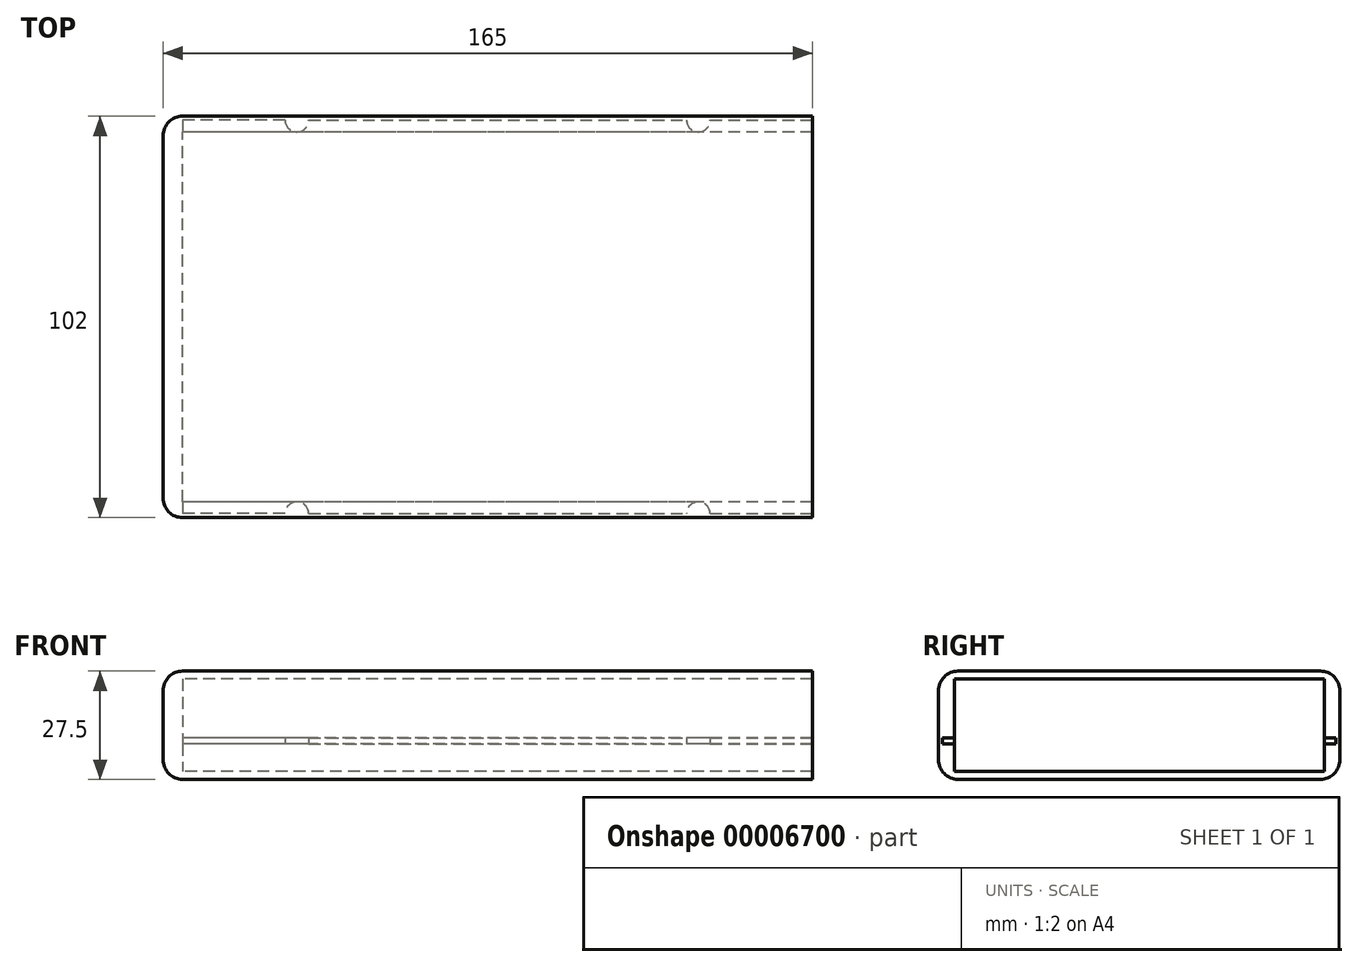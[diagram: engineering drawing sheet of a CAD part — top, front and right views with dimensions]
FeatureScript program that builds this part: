
annotation { "Feature Type Name" : "Feature", "Feature Type Description" : "" }
export const myFeature = defineFeature(function(context is Context, id is Id, definition is map)
    precondition{}
    {
        {
            var Q0;
            Q0=qCreatedBy(makeId("Top.planeOp"),FACE);
            var sketch = newSketch(context, id + "F0", { "sketchPlane" : qUnion([Q0])});
            skLineSegment(sketch, "E0.left", {"start": v(-80, 50) * mm, "end": v(-80, -50) * mm});
            skLineSegment(sketch, "E0.right", {"start": v(80, 50) * mm, "end": v(80, -50) * mm});
            skLineSegment(sketch, "E1.bottom", {"start": v(-87, -17.5) * mm, "end": v(-80, -17.5) * mm});
            skLineSegment(sketch, "E1.top", {"start": v(-87, -33) * mm, "end": v(-80, -33) * mm});
            skLineSegment(sketch, "E1.left", {"start": v(-87, -17.5) * mm, "end": v(-87, -33) * mm});
            skLineSegment(sketch, "E1.right", {"start": v(-80, -17.5) * mm, "end": v(-80, -33) * mm});
            skArc(sketch, "E2", {"start": v(54, 50) * mm, "mid": v(51, 47) * mm, "end": v(48, 50) * mm});
            skLineSegment(sketch, "E3", {"start": v(54, 50) * mm, "end": v(80, 50) * mm});
            skArc(sketch, "E4.MirrorCS", {"start": v(-54, 50) * mm, "mid": v(-51, 47) * mm, "end": v(-48, 50) * mm});
            skLineSegment(sketch, "E5.MirrorCS", {"start": v(-54, 50) * mm, "end": v(-80, 50) * mm});
            skLineSegment(sketch, "E6", {"start": v(-48, 50) * mm, "end": v(48, 50) * mm});
            skLineSegment(sketch, "E7.MirrorCS", {"start": v(54, -50) * mm, "end": v(80, -50) * mm});
            skArc(sketch, "E8.MirrorCS", {"start": v(54, -50) * mm, "mid": v(51, -47) * mm, "end": v(48, -50) * mm});
            skLineSegment(sketch, "E9.MirrorCS", {"start": v(-48, -50) * mm, "end": v(48, -50) * mm});
            skArc(sketch, "E10.MirrorCS", {"start": v(-54, -50) * mm, "mid": v(-51, -47) * mm, "end": v(-48, -50) * mm});
            skLineSegment(sketch, "E11.MirrorCS", {"start": v(-54, -50) * mm, "end": v(-80, -50) * mm});
            skLineSegment(sketch, "E12", {"start": v(48, 50) * mm, "end": v(54, 50) * mm, "construction": true});
            skSolve(sketch);
        }
        {
            var Q0;
            Q0=makeQuery(id+"F0.imprint","IMPRINT",FACE,{"disambiguationData":[TD([[makeQuery(id+"F0.imprint","IMPRINT",EDGE,{"derivedFrom":sQuery(id+"F0.wireOp",EDGE,"E0.right")}),-1.0]])]});
            extrude(context, id + "F1", {"entities" : qUnion([Q0]), "depth" : 1.5 * mm});
        }
        {
            var Q0;
            Q0=qCreatedBy(makeId("Right.planeOp"),FACE);
            var sketch = newSketch(context, id + "F2", { "sketchPlane" : qUnion([Q0])});
            skLineSegment(sketch, "E13.bottom", {"start": v(-47, 16.5) * mm, "end": v(47, 16.5) * mm});
            skLineSegment(sketch, "E13.top", {"start": v(-47, -7) * mm, "end": v(47, -7) * mm});
            skLineSegment(sketch, "E13.left", {"start": v(-47, 16.5) * mm, "end": v(-47, -7) * mm});
            skLineSegment(sketch, "E13.right", {"start": v(47, 16.5) * mm, "end": v(47, -7) * mm});
            skSolve(sketch);
        }
        {
            var Q0;
            Q0=makeQuery(id+"F2.imprint","IMPRINT",FACE,{"disambiguationData":[TD([[makeQuery(id+"F2.imprint","IMPRINT",EDGE,{"derivedFrom":sQuery(id+"F2.wireOp",EDGE,"E13.bottom")}),-1.0]])]});
            var Q1;
            Q1=makeQuery(id+"F1.opExtrude","SWEPT_FACE",FACE,{"disambiguationData":[OSD([sQuery(id+"F0.wireOp",EDGE,"E0.right")])]});
            var Q2;
            Q2=makeQuery(id+"F1.opExtrude","SWEPT_FACE",FACE,{"disambiguationData":[OSD([sQuery(id+"F0.wireOp",EDGE,"E0.left"),sQuery(id+"F0.wireOp",EDGE,"E1.right")])]});
            extrude(context, id + "F3", {"entities" : qUnion([Q0]), "endBound" : BoundingType.UP_TO_SURFACE, "endBoundEntityFace" : qUnion([Q1]), "depth" : 25 * mm, "hasSecondDirection" : true, "secondDirectionBound" : SecondDirectionBoundingType.UP_TO_SURFACE, "secondDirectionOppositeDirection" : true, "secondDirectionBoundEntityFace" : qUnion([Q2]), "secondDirectionDepth" : 25 * mm});
        }
        {
            var Q0;
            Q0=makeQuery(id+"F3.opExtrude","CAP_FACE",FACE,{"disambiguationData":[OSD([sQuery(id+"F2.wireOp",EDGE,"E13.bottom"),sQuery(id+"F2.wireOp",EDGE,"E13.top"),sQuery(id+"F2.wireOp",EDGE,"E13.left"),sQuery(id+"F2.wireOp",EDGE,"E13.right")])],"isStart":false});
            var sketch = newSketch(context, id + "F4", { "sketchPlane" : qUnion([Q0])});
            skLineSegment(sketch, "E14.bottom", {"start": v(-46, 18.5) * mm, "end": v(46, 18.5) * mm});
            skLineSegment(sketch, "E14.left", {"start": v(-51, 13.5) * mm, "end": v(-51, -4) * mm});
            skPoint(sketch, "E15.visualSharp", {"position": v(-51, 18.5) * mm});
            skArc(sketch, "E15.filletArc", {"start": v(-46, 18.5) * mm, "mid": v(-49.54, 17.04) * mm, "end": v(-51, 13.5) * mm});
            skArc(sketch, "E16.MirrorCS", {"start": v(46, 18.5) * mm, "mid": v(49.54, 17.04) * mm, "end": v(51, 13.5) * mm});
            skLineSegment(sketch, "E17.MirrorCS", {"start": v(-46, -9) * mm, "end": v(46, -9) * mm});
            skPoint(sketch, "E18.visualSharp", {"position": v(-51, -9) * mm});
            skArc(sketch, "E18.filletArc", {"start": v(-51, -4) * mm, "mid": v(-49.54, -7.54) * mm, "end": v(-46, -9) * mm});
            skLineSegment(sketch, "E19.MirrorCS", {"start": v(51, 13.5) * mm, "end": v(51, -4) * mm});
            skArc(sketch, "E20.MirrorCS", {"start": v(51, -4) * mm, "mid": v(49.54, -7.54) * mm, "end": v(46, -9) * mm});
            skSolve(sketch);
        }
        {
            var Q0;
            Q0 = qSketchRegion(id + "F4", true);
            extrude(context, id + "F5", {"entities" : qUnion([Q0]), "oppositeDirection" : true, "depth" : 165 * mm});
        }
        {
            var Q0;
            Q0=makeQuery(id+"F1.opExtrude","SWEPT_BODY",BODY,{"disambiguationData":[OSD([sQuery(id+"F0.wireOp",EDGE,"E0.left"),sQuery(id+"F0.wireOp",EDGE,"E0.right"),sQuery(id+"F0.wireOp",EDGE,"E1.right"),sQuery(id+"F0.wireOp",EDGE,"E2"),sQuery(id+"F0.wireOp",EDGE,"E3"),sQuery(id+"F0.wireOp",EDGE,"E4.MirrorCS"),sQuery(id+"F0.wireOp",EDGE,"E5.MirrorCS"),sQuery(id+"F0.wireOp",EDGE,"E6"),sQuery(id+"F0.wireOp",EDGE,"E7.MirrorCS"),sQuery(id+"F0.wireOp",EDGE,"E8.MirrorCS"),sQuery(id+"F0.wireOp",EDGE,"E9.MirrorCS"),sQuery(id+"F0.wireOp",EDGE,"E10.MirrorCS"),sQuery(id+"F0.wireOp",EDGE,"E11.MirrorCS")])]});
            var Q1;
            Q1=makeQuery(id+"F3.opExtrude","SWEPT_BODY",BODY,{"disambiguationData":[OSD([sQuery(id+"F2.wireOp",EDGE,"E13.bottom"),sQuery(id+"F2.wireOp",EDGE,"E13.top"),sQuery(id+"F2.wireOp",EDGE,"E13.left"),sQuery(id+"F2.wireOp",EDGE,"E13.right")])]});
            var Q2;
            Q2=makeQuery(id+"F5.opExtrude","SWEPT_BODY",BODY,{"disambiguationData":[OSD([sQuery(id+"F4.wireOp",EDGE,"E14.bottom"),sQuery(id+"F4.wireOp",EDGE,"E14.left"),sQuery(id+"F4.wireOp",EDGE,"E15.filletArc"),sQuery(id+"F4.wireOp",EDGE,"E16.MirrorCS"),sQuery(id+"F4.wireOp",EDGE,"E17.MirrorCS"),sQuery(id+"F4.wireOp",EDGE,"E18.filletArc"),sQuery(id+"F4.wireOp",EDGE,"E19.MirrorCS"),sQuery(id+"F4.wireOp",EDGE,"E20.MirrorCS")])]});
            booleanBodies(context, id + "F6", {"operationType" : BooleanOperationType.SUBTRACTION, "tools" : qUnion([Q0, Q1]), "targets" : qUnion([Q2])});
        }
        {
            var Q0;
            Q0=makeQuery(id+"F5.opExtrude","CAP_EDGE",EDGE,{"disambiguationData":[OSD([sQuery(id+"F4.wireOp",EDGE,"E14.bottom")])],"isStart":false});
            fillet(context, id + "F7", {"entities" : qUnion([Q0]), "radius" : 5 * mm, "tangentPropagation" : true, "allowEdgeOverflow" : false});
        }
    });
